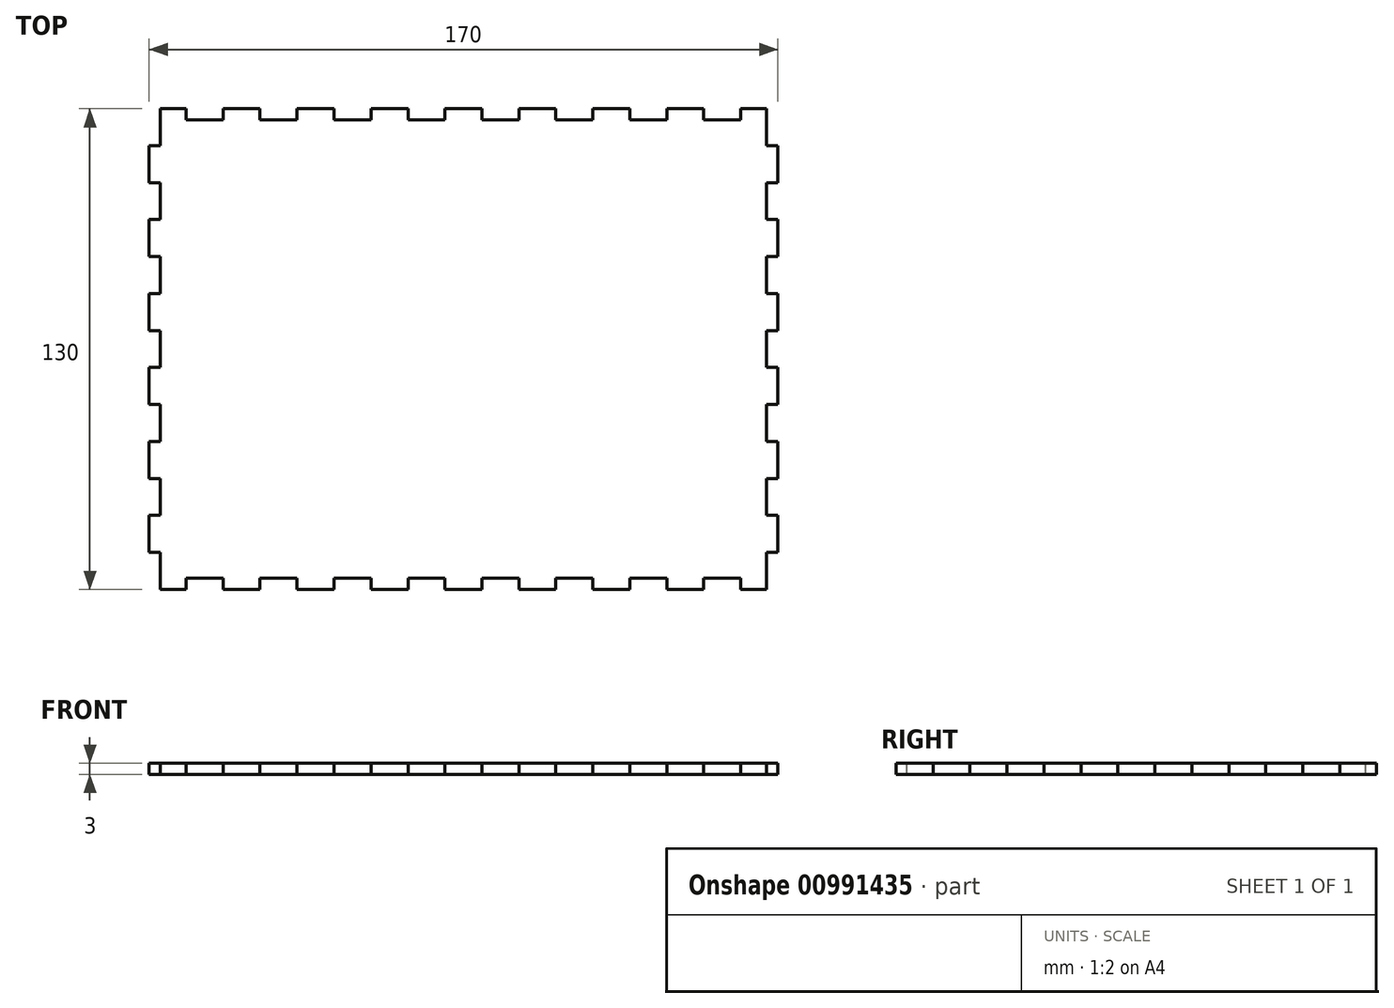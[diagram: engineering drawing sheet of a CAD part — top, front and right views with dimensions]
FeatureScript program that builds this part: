
annotation { "Feature Type Name" : "Feature", "Feature Type Description" : "" }
export const myFeature = defineFeature(function(context is Context, id is Id, definition is map)
    precondition{}
    {
        {
            var Q0;
            Q0=qCreatedBy(makeId("Top.planeOp"),FACE);
            var sketch = newSketch(context, id + "F0", { "sketchPlane" : qUnion([Q0])});
            skLineSegment(sketch, "E0.bottom", {"start": v(85, -65) * mm, "end": v(-85, -65) * mm});
            skLineSegment(sketch, "E0.top", {"start": v(85, 65) * mm, "end": v(-85, 65) * mm});
            skLineSegment(sketch, "E0.left", {"start": v(85, -65) * mm, "end": v(85, 65) * mm});
            skLineSegment(sketch, "E0.right", {"start": v(-85, -65) * mm, "end": v(-85, 65) * mm});
            skPoint(sketch, "E0.middle", {"position": v(0, 0) * mm});
            skSolve(sketch);
        }
        {
            var Q0;
            Q0 = qSketchRegion(id + "F0", true);
            extrude(context, id + "F1", {"entities" : qUnion([Q0]), "depth" : 3 * mm, "offsetDistance" : 25 * mm});
        }
        {
            var Q0;
            Q0=makeQuery(id+"F1.opExtrude","CAP_FACE",FACE,{"disambiguationData":[OSD([sQuery(id+"F0.wireOp",EDGE,"E0.bottom"),sQuery(id+"F0.wireOp",EDGE,"E0.top"),sQuery(id+"F0.wireOp",EDGE,"E0.left"),sQuery(id+"F0.wireOp",EDGE,"E0.right")])],"isStart":false});
            var sketch = newSketch(context, id + "F2", { "sketchPlane" : qUnion([Q0])});
            skLineSegment(sketch, "E1.bottom", {"start": v(-75, -65) * mm, "end": v(-65, -65) * mm});
            skLineSegment(sketch, "E1.top", {"start": v(-75, -62) * mm, "end": v(-65, -62) * mm});
            skLineSegment(sketch, "E1.left", {"start": v(-75, -65) * mm, "end": v(-75, -62) * mm});
            skLineSegment(sketch, "E1.right", {"start": v(-65, -65) * mm, "end": v(-65, -62) * mm});
            skLineSegment(sketch, "E2.1.0.0", {"start": v(-55, -65) * mm, "end": v(-45, -65) * mm});
            skLineSegment(sketch, "E2.1.0.1", {"start": v(-55, -62) * mm, "end": v(-45, -62) * mm});
            skLineSegment(sketch, "E2.1.0.2", {"start": v(-55, -65) * mm, "end": v(-55, -62) * mm});
            skLineSegment(sketch, "E2.1.0.3", {"start": v(-45, -65) * mm, "end": v(-45, -62) * mm});
            skLineSegment(sketch, "E2.2.0.0", {"start": v(-35, -65) * mm, "end": v(-25, -65) * mm});
            skLineSegment(sketch, "E2.2.0.1", {"start": v(-35, -62) * mm, "end": v(-25, -62) * mm});
            skLineSegment(sketch, "E2.2.0.2", {"start": v(-35, -65) * mm, "end": v(-35, -62) * mm});
            skLineSegment(sketch, "E2.2.0.3", {"start": v(-25, -65) * mm, "end": v(-25, -62) * mm});
            skLineSegment(sketch, "E2.3.0.0", {"start": v(-15, -65) * mm, "end": v(-5, -65) * mm});
            skLineSegment(sketch, "E2.3.0.1", {"start": v(-15, -62) * mm, "end": v(-5, -62) * mm});
            skLineSegment(sketch, "E2.3.0.2", {"start": v(-15, -65) * mm, "end": v(-15, -62) * mm});
            skLineSegment(sketch, "E2.3.0.3", {"start": v(-5, -65) * mm, "end": v(-5, -62) * mm});
            skLineSegment(sketch, "E2.4.0.0", {"start": v(5, -65) * mm, "end": v(15, -65) * mm});
            skLineSegment(sketch, "E2.4.0.1", {"start": v(5, -62) * mm, "end": v(15, -62) * mm});
            skLineSegment(sketch, "E2.4.0.2", {"start": v(5, -65) * mm, "end": v(5, -62) * mm});
            skLineSegment(sketch, "E2.4.0.3", {"start": v(15, -65) * mm, "end": v(15, -62) * mm});
            skLineSegment(sketch, "E2.5.0.0", {"start": v(25, -65) * mm, "end": v(35, -65) * mm});
            skLineSegment(sketch, "E2.5.0.1", {"start": v(25, -62) * mm, "end": v(35, -62) * mm});
            skLineSegment(sketch, "E2.5.0.2", {"start": v(25, -65) * mm, "end": v(25, -62) * mm});
            skLineSegment(sketch, "E2.5.0.3", {"start": v(35, -65) * mm, "end": v(35, -62) * mm});
            skLineSegment(sketch, "E2.6.0.0", {"start": v(45, -65) * mm, "end": v(55, -65) * mm});
            skLineSegment(sketch, "E2.6.0.1", {"start": v(45, -62) * mm, "end": v(55, -62) * mm});
            skLineSegment(sketch, "E2.6.0.2", {"start": v(45, -65) * mm, "end": v(45, -62) * mm});
            skLineSegment(sketch, "E2.6.0.3", {"start": v(55, -65) * mm, "end": v(55, -62) * mm});
            skLineSegment(sketch, "E2.7.0.0", {"start": v(65, -65) * mm, "end": v(75, -65) * mm});
            skLineSegment(sketch, "E2.7.0.1", {"start": v(65, -62) * mm, "end": v(75, -62) * mm});
            skLineSegment(sketch, "E2.7.0.2", {"start": v(65, -65) * mm, "end": v(65, -62) * mm});
            skLineSegment(sketch, "E2.7.0.3", {"start": v(75, -65) * mm, "end": v(75, -62) * mm});
            skLineSegment(sketch, "E2.direction1", {"start": v(-75, -65) * mm, "end": v(-55, -65) * mm, "construction": true});
            skLineSegment(sketch, "E3.bottom", {"start": v(-85, -65) * mm, "end": v(-82, -65) * mm});
            skLineSegment(sketch, "E3.top", {"start": v(-85, -55) * mm, "end": v(-82, -55) * mm});
            skLineSegment(sketch, "E3.left", {"start": v(-85, -65) * mm, "end": v(-85, -55) * mm});
            skLineSegment(sketch, "E3.right", {"start": v(-82, -65) * mm, "end": v(-82, -55) * mm});
            skLineSegment(sketch, "E4.0.1.0", {"start": v(-85, -45) * mm, "end": v(-82, -45) * mm});
            skLineSegment(sketch, "E4.0.1.1", {"start": v(-85, -35) * mm, "end": v(-82, -35) * mm});
            skLineSegment(sketch, "E4.0.1.2", {"start": v(-85, -45) * mm, "end": v(-85, -35) * mm});
            skLineSegment(sketch, "E4.0.1.3", {"start": v(-82, -45) * mm, "end": v(-82, -35) * mm});
            skLineSegment(sketch, "E4.0.2.0", {"start": v(-85, -25) * mm, "end": v(-82, -25) * mm});
            skLineSegment(sketch, "E4.0.2.1", {"start": v(-85, -15) * mm, "end": v(-82, -15) * mm});
            skLineSegment(sketch, "E4.0.2.2", {"start": v(-85, -25) * mm, "end": v(-85, -15) * mm});
            skLineSegment(sketch, "E4.0.2.3", {"start": v(-82, -25) * mm, "end": v(-82, -15) * mm});
            skLineSegment(sketch, "E4.0.3.0", {"start": v(-85, -5) * mm, "end": v(-82, -5) * mm});
            skLineSegment(sketch, "E4.0.3.1", {"start": v(-85, 5) * mm, "end": v(-82, 5) * mm});
            skLineSegment(sketch, "E4.0.3.2", {"start": v(-85, -5) * mm, "end": v(-85, 5) * mm});
            skLineSegment(sketch, "E4.0.3.3", {"start": v(-82, -5) * mm, "end": v(-82, 5) * mm});
            skLineSegment(sketch, "E4.0.4.0", {"start": v(-85, 15) * mm, "end": v(-82, 15) * mm});
            skLineSegment(sketch, "E4.0.4.1", {"start": v(-85, 25) * mm, "end": v(-82, 25) * mm});
            skLineSegment(sketch, "E4.0.4.2", {"start": v(-85, 15) * mm, "end": v(-85, 25) * mm});
            skLineSegment(sketch, "E4.0.4.3", {"start": v(-82, 15) * mm, "end": v(-82, 25) * mm});
            skLineSegment(sketch, "E4.0.5.0", {"start": v(-85, 35) * mm, "end": v(-82, 35) * mm});
            skLineSegment(sketch, "E4.0.5.1", {"start": v(-85, 45) * mm, "end": v(-82, 45) * mm});
            skLineSegment(sketch, "E4.0.5.2", {"start": v(-85, 35) * mm, "end": v(-85, 45) * mm});
            skLineSegment(sketch, "E4.0.5.3", {"start": v(-82, 35) * mm, "end": v(-82, 45) * mm});
            skLineSegment(sketch, "E4.0.6.0", {"start": v(-85, 55) * mm, "end": v(-82, 55) * mm});
            skLineSegment(sketch, "E4.0.6.1", {"start": v(-85, 65) * mm, "end": v(-82, 65) * mm});
            skLineSegment(sketch, "E4.0.6.2", {"start": v(-85, 55) * mm, "end": v(-85, 65) * mm});
            skLineSegment(sketch, "E4.0.6.3", {"start": v(-82, 55) * mm, "end": v(-82, 65) * mm});
            skLineSegment(sketch, "E4.direction1", {"start": v(-85, -65) * mm, "end": v(-60, -65) * mm, "construction": true});
            skLineSegment(sketch, "E4.direction2", {"start": v(-85, -65) * mm, "end": v(-85, -45) * mm, "construction": true});
            skLineSegment(sketch, "E5", {"start": v(85, 0) * mm, "end": v(-85, 0) * mm, "construction": true});
            skLineSegment(sketch, "E6", {"start": v(0, 65) * mm, "end": v(0, -65) * mm, "construction": true});
            skLineSegment(sketch, "E7.MirrorCS", {"start": v(85, -65) * mm, "end": v(85, -55) * mm});
            skLineSegment(sketch, "E8.MirrorCS", {"start": v(82, -45) * mm, "end": v(82, -35) * mm});
            skLineSegment(sketch, "E9.MirrorCS", {"start": v(85, -45) * mm, "end": v(85, -35) * mm});
            skLineSegment(sketch, "E10.MirrorCS", {"start": v(82, 15) * mm, "end": v(82, 25) * mm});
            skLineSegment(sketch, "E11.MirrorCS", {"start": v(85, 15) * mm, "end": v(85, 25) * mm});
            skLineSegment(sketch, "E12.MirrorCS", {"start": v(85, 55) * mm, "end": v(82, 55) * mm});
            skLineSegment(sketch, "E13.MirrorCS", {"start": v(85, -5) * mm, "end": v(85, 5) * mm});
            skLineSegment(sketch, "E14.MirrorCS", {"start": v(85, 55) * mm, "end": v(85, 65) * mm});
            skLineSegment(sketch, "E15.MirrorCS", {"start": v(85, -5) * mm, "end": v(82, -5) * mm});
            skLineSegment(sketch, "E16.MirrorCS", {"start": v(85, 65) * mm, "end": v(82, 65) * mm});
            skLineSegment(sketch, "E17.MirrorCS", {"start": v(82, 55) * mm, "end": v(82, 65) * mm});
            skLineSegment(sketch, "E18.MirrorCS", {"start": v(85, 15) * mm, "end": v(82, 15) * mm});
            skLineSegment(sketch, "E19.MirrorCS", {"start": v(85, -25) * mm, "end": v(85, -15) * mm});
            skLineSegment(sketch, "E20.MirrorCS", {"start": v(82, -5) * mm, "end": v(82, 5) * mm});
            skLineSegment(sketch, "E21.MirrorCS", {"start": v(85, -35) * mm, "end": v(82, -35) * mm});
            skLineSegment(sketch, "E22.MirrorCS", {"start": v(85, -55) * mm, "end": v(82, -55) * mm});
            skLineSegment(sketch, "E23.MirrorCS", {"start": v(85, -45) * mm, "end": v(82, -45) * mm});
            skLineSegment(sketch, "E24.MirrorCS", {"start": v(85, 25) * mm, "end": v(82, 25) * mm});
            skLineSegment(sketch, "E25.MirrorCS", {"start": v(85, 35) * mm, "end": v(82, 35) * mm});
            skLineSegment(sketch, "E26.MirrorCS", {"start": v(85, 5) * mm, "end": v(82, 5) * mm});
            skLineSegment(sketch, "E27.MirrorCS", {"start": v(82, -65) * mm, "end": v(82, -55) * mm});
            skLineSegment(sketch, "E28.MirrorCS", {"start": v(85, -15) * mm, "end": v(82, -15) * mm});
            skLineSegment(sketch, "E29.MirrorCS", {"start": v(85, -65) * mm, "end": v(85, -45) * mm, "construction": true});
            skLineSegment(sketch, "E30.MirrorCS", {"start": v(85, 45) * mm, "end": v(82, 45) * mm});
            skLineSegment(sketch, "E31.MirrorCS", {"start": v(82, 35) * mm, "end": v(82, 45) * mm});
            skLineSegment(sketch, "E32.MirrorCS", {"start": v(85, 35) * mm, "end": v(85, 45) * mm});
            skLineSegment(sketch, "E33.MirrorCS", {"start": v(85, -25) * mm, "end": v(82, -25) * mm});
            skLineSegment(sketch, "E34.MirrorCS", {"start": v(82, -25) * mm, "end": v(82, -15) * mm});
            skLineSegment(sketch, "E35.MirrorCS", {"start": v(85, -65) * mm, "end": v(82, -65) * mm});
            skLineSegment(sketch, "E36.MirrorCS", {"start": v(15, 65) * mm, "end": v(15, 62) * mm});
            skLineSegment(sketch, "E37.MirrorCS", {"start": v(-65, 65) * mm, "end": v(-65, 62) * mm});
            skLineSegment(sketch, "E38.MirrorCS", {"start": v(45, 65) * mm, "end": v(45, 62) * mm});
            skLineSegment(sketch, "E39.MirrorCS", {"start": v(5, 65) * mm, "end": v(5, 62) * mm});
            skLineSegment(sketch, "E40.MirrorCS", {"start": v(75, 65) * mm, "end": v(75, 62) * mm});
            skLineSegment(sketch, "E41.MirrorCS", {"start": v(-35, 65) * mm, "end": v(-35, 62) * mm});
            skLineSegment(sketch, "E42.MirrorCS", {"start": v(65, 65) * mm, "end": v(65, 62) * mm});
            skLineSegment(sketch, "E43.MirrorCS", {"start": v(-45, 65) * mm, "end": v(-45, 62) * mm});
            skLineSegment(sketch, "E44.MirrorCS", {"start": v(35, 65) * mm, "end": v(35, 62) * mm});
            skLineSegment(sketch, "E45.MirrorCS", {"start": v(-75, 65) * mm, "end": v(-75, 62) * mm});
            skLineSegment(sketch, "E46.MirrorCS", {"start": v(-15, 65) * mm, "end": v(-15, 62) * mm});
            skLineSegment(sketch, "E47.MirrorCS", {"start": v(55, 65) * mm, "end": v(55, 62) * mm});
            skLineSegment(sketch, "E48.MirrorCS", {"start": v(-5, 65) * mm, "end": v(-5, 62) * mm});
            skLineSegment(sketch, "E49.MirrorCS", {"start": v(25, 65) * mm, "end": v(25, 62) * mm});
            skLineSegment(sketch, "E50.MirrorCS", {"start": v(-25, 65) * mm, "end": v(-25, 62) * mm});
            skLineSegment(sketch, "E51.MirrorCS", {"start": v(-55, 65) * mm, "end": v(-55, 62) * mm});
            skLineSegment(sketch, "E52.MirrorCS", {"start": v(-75, 65) * mm, "end": v(-65, 65) * mm});
            skLineSegment(sketch, "E53.MirrorCS", {"start": v(25, 65) * mm, "end": v(35, 65) * mm});
            skLineSegment(sketch, "E54.MirrorCS", {"start": v(5, 65) * mm, "end": v(15, 65) * mm});
            skLineSegment(sketch, "E55.MirrorCS", {"start": v(-55, 62) * mm, "end": v(-45, 62) * mm});
            skLineSegment(sketch, "E56.MirrorCS", {"start": v(5, 62) * mm, "end": v(15, 62) * mm});
            skLineSegment(sketch, "E57.MirrorCS", {"start": v(-55, 65) * mm, "end": v(-45, 65) * mm});
            skLineSegment(sketch, "E58.MirrorCS", {"start": v(65, 62) * mm, "end": v(75, 62) * mm});
            skLineSegment(sketch, "E59.MirrorCS", {"start": v(-15, 62) * mm, "end": v(-5, 62) * mm});
            skLineSegment(sketch, "E60.MirrorCS", {"start": v(-35, 62) * mm, "end": v(-25, 62) * mm});
            skLineSegment(sketch, "E61.MirrorCS", {"start": v(-75, 65) * mm, "end": v(-55, 65) * mm, "construction": true});
            skLineSegment(sketch, "E62.MirrorCS", {"start": v(-35, 65) * mm, "end": v(-25, 65) * mm});
            skLineSegment(sketch, "E63.MirrorCS", {"start": v(45, 62) * mm, "end": v(55, 62) * mm});
            skLineSegment(sketch, "E64.MirrorCS", {"start": v(-15, 65) * mm, "end": v(-5, 65) * mm});
            skLineSegment(sketch, "E65.MirrorCS", {"start": v(-75, 62) * mm, "end": v(-65, 62) * mm});
            skLineSegment(sketch, "E66.MirrorCS", {"start": v(45, 65) * mm, "end": v(55, 65) * mm});
            skLineSegment(sketch, "E67.MirrorCS", {"start": v(25, 62) * mm, "end": v(35, 62) * mm});
            skLineSegment(sketch, "E68.MirrorCS", {"start": v(65, 65) * mm, "end": v(75, 65) * mm});
            skSolve(sketch);
        }
        {
            var Q0;
            Q0 = qSketchRegion(id + "F2", true);
            extrude(context, id + "F3", {"entities" : qUnion([Q0]), "operationType" : NewBodyOperationType.REMOVE, "endBound" : BoundingType.THROUGH_ALL, "oppositeDirection" : true, "depth" : 25 * mm, "offsetDistance" : 25 * mm});
        }
    });
